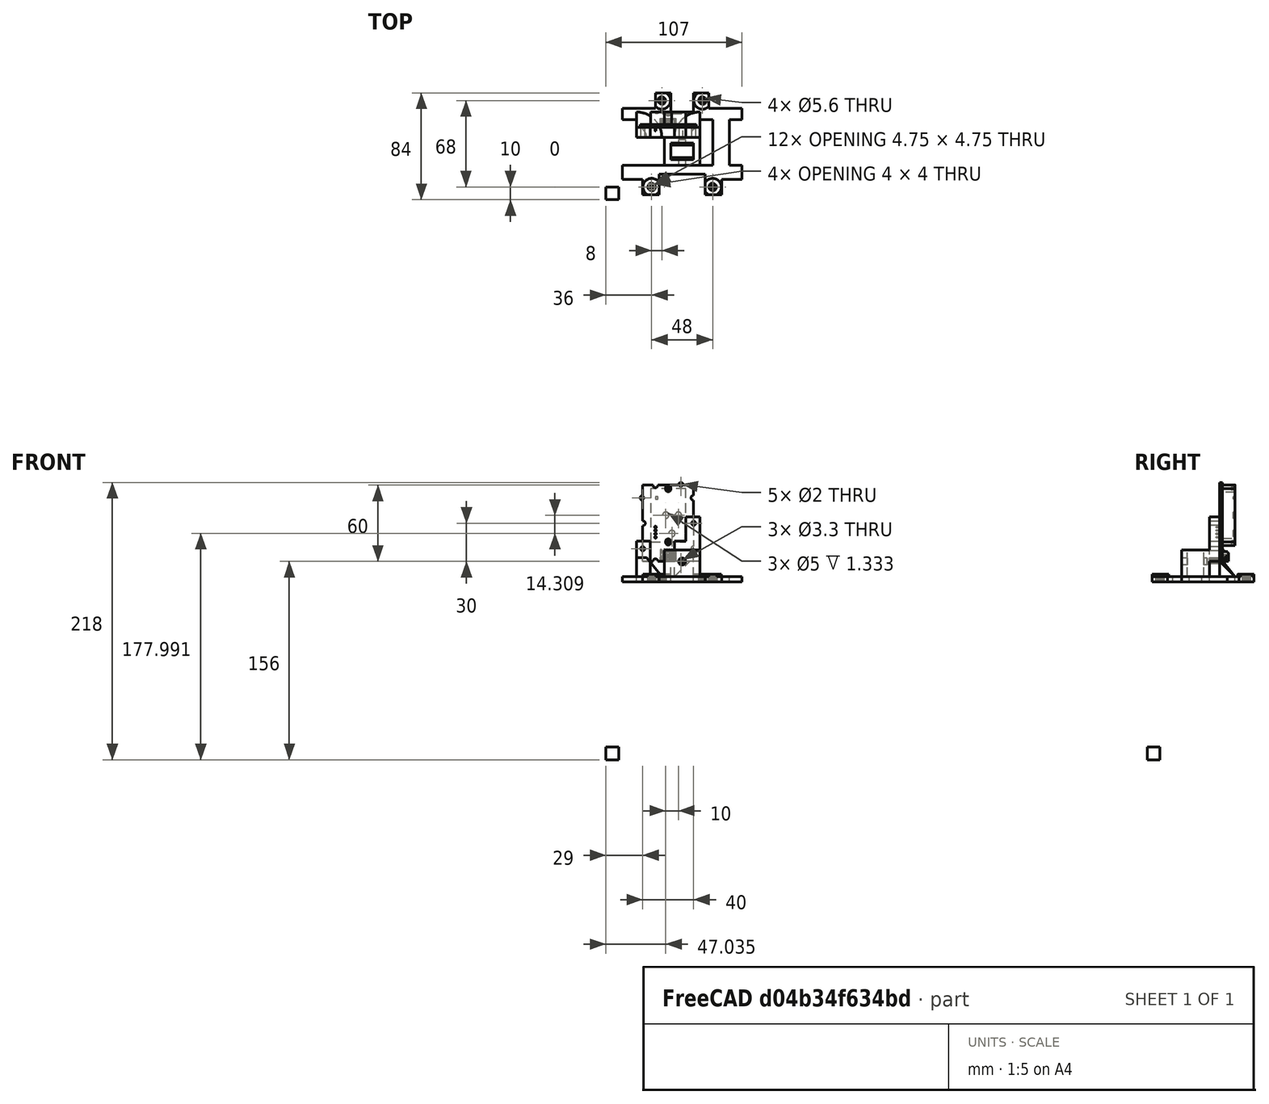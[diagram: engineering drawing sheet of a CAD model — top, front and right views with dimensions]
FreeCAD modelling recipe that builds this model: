
FCSTD DOCUMENT  (FreeCAD 0.20R29177 (Git))
Label: spin07122022
License: All rights reserved
LicenseURL: http://en.wikipedia.org/wiki/All_rights_reserved
objects: Part::Box×23, Part::Cylinder×17, Part::MultiFuse×12, Part::Feature×5, Part::Cut×3, Part::Cone×2
note: 62 computed .brp shape members not serialized (recipe doc carries the construction recipe); baked Part::Feature solids carry a one-line shape summary decoded from their .brp

FEATURE [Part::Cylinder] Cylinder103  label="Cylinder107"
  Angle = 360
  AttacherType = Attacher::AttachEngine3D
  FirstAngle = 0
  Height = 10
  Placement = pos=(63,3,0) rot=(0,0,1;0rad)
  Radius = 2.25
  SecondAngle = 0
FEATURE [Part::Box] Box064  label="base005"
  AttacherType = Attacher::AttachEngine3D
  Height = 4
  Length = 26
  Placement = pos=(-10.25,68,0) rot=(0,0,1;0rad)
  Width = 12
FEATURE [Part::Box] Box060  label="base001"
  AttacherType = Attacher::AttachEngine3D
  Height = 4
  Length = 94
  Width = 80
FEATURE [Part::Box] Box061  label="base002"
  AttacherType = Attacher::AttachEngine3D
  Height = 4
  Length = 26
  Width = 12
FEATURE [Part::Box] Box062  label="base003"
  AttacherType = Attacher::AttachEngine3D
  Height = 4
  Length = 26
  Placement = pos=(68,0,0) rot=(0,0,1;0rad)
  Width = 12
FEATURE [Part::Cylinder] Cylinder104  label="Cylinder103"
  Angle = 360
  AttacherType = Attacher::AttachEngine3D
  FirstAngle = 0
  Height = 10
  Placement = pos=(71,71,0) rot=(0,0,1;0rad)
  Radius = 2.25
  SecondAngle = 0
FEATURE [Part::Cylinder] Cylinder106  label="Cylinder104"
  Angle = 360
  AttacherType = Attacher::AttachEngine3D
  FirstAngle = 0
  Height = 10
  Placement = pos=(23,71,0) rot=(0,0,1;0rad)
  Radius = 2
  SecondAngle = 0
FEATURE [Part::Cylinder] Cylinder105  label="Cylinder108"
  Angle = 360
  AttacherType = Attacher::AttachEngine3D
  FirstAngle = 0
  Height = 10
  Placement = pos=(31,3,0) rot=(0,0,1;0rad)
  Radius = 2.25
  SecondAngle = 0
FEATURE [Part::Box] Box081  label="Cube039"
  AttacherType = Attacher::AttachEngine3D
  Height = 10
  Length = 10
  Placement = pos=(74,27,140) rot=(0,0,1;0rad)
  Width = 36
FEATURE [Part::Box] Box082  label="Cube040"
  AttacherType = Attacher::AttachEngine3D
  Height = 10
  Length = 36
  Placement = pos=(42,1,140) rot=(0,0,1;0rad)
  Width = 19
FEATURE [Part::Box] Box073  label="baseSpineCut"
  AttacherType = Attacher::AttachEngine3D
  Height = 25
  Length = 18
  Placement = pos=(51,33,140) rot=(0,0,1;0rad)
  Width = 10
FEATURE [Part::Cylinder] Cylinder107  label="Cylinder109"
  Angle = 360
  AttacherType = Attacher::AttachEngine3D
  FirstAngle = 0
  Height = 10
  Radius = 1
  SecondAngle = 0
FEATURE [Part::MultiFuse] Fusion123  label="screwIns001"
  Placement = pos=(0,3,0) rot=(0,0,1;0rad)
  Shapes = -> [Cylinder105,Cylinder107,Cylinder103,Cylinder104,Cylinder106]
FEATURE [Part::Box] Box080  label="Cube038"
  AttacherType = Attacher::AttachEngine3D
  Height = 10
  Length = 33
  Placement = pos=(13,27,140) rot=(0,0,1;0rad)
  Width = 22
FEATURE [Part::Box] Box063  label="base004"
  AttacherType = Attacher::AttachEngine3D
  Height = 4
  Length = 26
  Placement = pos=(78,68,0) rot=(0,0,1;0rad)
  Width = 12
FEATURE [Part::MultiFuse] Fusion122
  Shapes = -> [Box064,Box063,Box061,Box062]
FEATURE [Part::Cut] Cut019  label="baseNew"
  Base = -> Box060
  Tool = -> Fusion122
FEATURE [Part::Cut] Cut020  label="baseNew001"
  Base = -> Cut019
  Placement = pos=(107,84,140) rot=(0,0,1;3.14159rad)
  Tool = -> Fusion123
FEATURE [Part::Box] Box083  label="Cube041"
  AttacherType = Attacher::AttachEngine3D
  Height = 25
  Length = 18
  Placement = pos=(51,31.5,144) rot=(0,0,1;0rad)
  Width = 13
FEATURE [Part::Box] Box084  label="Cube042"
  AttacherType = Attacher::AttachEngine3D
  Height = 51
  Length = 50
  Placement = pos=(24,49,140) rot=(0,0,1;0rad)
  Width = 8
FEATURE [Part::Box] Box085  label="Cube043"
  AttacherType = Attacher::AttachEngine3D
  Height = 10
  Length = 15
  Placement = pos=(69,69,140) rot=(0,0,1;1.5708rad)
  Width = 18
FEATURE [Part::Box] Box086  label="baseSpineIn"
  AttacherType = Attacher::AttachEngine3D
  Height = 25
  Length = 28
  Placement = pos=(46,27,140) rot=(0,0,1;0rad)
  Width = 22
FEATURE [Part::Cylinder] Cylinder
  Angle = 360
  AttacherType = Attacher::AttachEngine3D
  FirstAngle = 0
  Height = 50
  Placement = pos=(60,-3,156) rot=(-1,0,0;1.5708rad)
  Radius = 2.8
  SecondAngle = 0
FEATURE [Part::Feature] Feature  label="Seed Grove SCD30"
  Placement = pos=(29,59,156) rot=(0.707107,0,0.707107;3.14159rad)
  shape: bbox 44 x 15.1 x 64 mm, 422 faces, 13 solids (baked)
FEATURE [Part::Cylinder] Cylinder108  label="Cylinder110"
  Angle = 360
  AttacherType = Attacher::AttachEngine3D
  FirstAngle = 0
  Height = 50
  Placement = pos=(80,17,186) rot=(-1,0,0;1.5708rad)
  Radius = 1.65
  SecondAngle = 0
FEATURE [Part::Cylinder] Cylinder109  label="Cylinder111"
  Angle = 360
  AttacherType = Attacher::AttachEngine3D
  FirstAngle = 0
  Height = 50
  Placement = pos=(40,17,166) rot=(-1,0,0;1.5708rad)
  Radius = 1.65
  SecondAngle = 0
FEATURE [Part::Cylinder] Cylinder110  label="Cylinder112"
  Angle = 360
  AttacherType = Attacher::AttachEngine3D
  FirstAngle = 0
  Height = 50
  Placement = pos=(70,17,156) rot=(-1,0,0;1.5708rad)
  Radius = 1.65
  SecondAngle = 0
FEATURE [Part::MultiFuse] Fusion  label="m2Cuts"
  Placement = pos=(-11,30,0) rot=(0,0,1;0rad)
  Shapes = -> [Cylinder108,Cylinder109,Cylinder110]
FEATURE [Part::Box] Box087  label="Cube044"
  AttacherType = Attacher::AttachEngine3D
  Height = 51
  Length = 50
  Placement = pos=(13,49,172) rot=(0,0,1;0rad)
  Width = 8
FEATURE [Part::Box] Box088  label="Cube045"
  AttacherType = Attacher::AttachEngine3D
  Height = 51
  Length = 19
  Placement = pos=(35,49,144) rot=(0,0,1;0rad)
  Width = 8
FEATURE [Part::MultiFuse] Fusion124  label="base"
  Shapes = -> [Cut020,Box084,Box086]
FEATURE [Part::MultiFuse] Fusion125  label="cuts"
  Shapes = -> [Box087,Box088,Fusion,Box085,Box080,Box083,Box082,Box081,Box073,Cylinder]
FEATURE [Part::Box] Box089  label="Cube046"
  AttacherType = Attacher::AttachEngine3D
  Height = 10
  Length = 11
  Placement = pos=(13,57,140) rot=(0,0,1;0rad)
  Width = 6
FEATURE [Part::Feature] Solid  label="m4HeatSet"
  Placement = pos=(36,10,140) rot=(1,0,0;1.5708rad)
  shape: bbox 7.1 x 7.1 x 6.065 mm, 234 faces (baked)
FEATURE [Part::Feature] Solid001  label="m4HeatSet001"
  Placement = pos=(84,10,140) rot=(1,0,0;1.5708rad)
  shape: bbox 7.1 x 7.1 x 6.065 mm, 234 faces (baked)
FEATURE [Part::Feature] Solid002  label="m4HeatSet002"
  Placement = pos=(44,78,140) rot=(1,0,0;1.5708rad)
  shape: bbox 7.1 x 7.1 x 6.065 mm, 234 faces (baked)
FEATURE [Part::Feature] Solid003  label="m4HeatSet003"
  Placement = pos=(76,78,140) rot=(1,0,0;1.5708rad)
  shape: bbox 7.1 x 7.1 x 6.065 mm, 234 faces (baked)
FEATURE [Part::Cylinder] Cylinder111  label="m4HeatSetCut"
  Angle = 360
  AttacherType = Attacher::AttachEngine3D
  FirstAngle = 0
  Height = 10
  Placement = pos=(36,10,140) rot=(0,0,1;0rad)
  Radius = 2.8
  SecondAngle = 0
FEATURE [Part::Cylinder] Cylinder112  label="m4HeatSetCut001"
  Angle = 360
  AttacherType = Attacher::AttachEngine3D
  FirstAngle = 0
  Height = 10
  Placement = pos=(84,10,140) rot=(0,0,1;0rad)
  Radius = 2.8
  SecondAngle = 0
FEATURE [Part::Cylinder] Cylinder113  label="m4HeatSetCut002"
  Angle = 360
  AttacherType = Attacher::AttachEngine3D
  FirstAngle = 0
  Height = 10
  Placement = pos=(76,78,140) rot=(0,0,1;0rad)
  Radius = 2.8
  SecondAngle = 0
FEATURE [Part::Cylinder] Cylinder114  label="m4HeatSetCut003"
  Angle = 360
  AttacherType = Attacher::AttachEngine3D
  FirstAngle = 0
  Height = 10
  Placement = pos=(44,78,140) rot=(0,0,1;0rad)
  Radius = 2.8
  SecondAngle = 0
FEATURE [Part::MultiFuse] Fusion126  label="heatSetCuts"
  Shapes = -> [Cylinder111,Cylinder112,Cylinder113,Cylinder114]
FEATURE [Part::Box] Box091  label="Cube048"
  AttacherType = Attacher::AttachEngine3D
  Height = 10
  Length = 11
  Placement = pos=(13,49,140) rot=(0,0,1;0rad)
  Width = 8
FEATURE [Part::MultiFuse] Fusion127  label="cuts001"
  Shapes = -> [Box091,Fusion126,Box089,Fusion125]
FEATURE [Part::Cylinder] Cylinder115  label="m4HeatSetCut004"
  Angle = 360
  AttacherType = Attacher::AttachEngine3D
  FirstAngle = 0
  Height = 6
  Placement = pos=(36,10,140) rot=(0,0,-1;1.0472rad)
  Radius = 6.8
  SecondAngle = 0
FEATURE [Part::Cylinder] Cylinder116  label="m4HeatSetCut005"
  Angle = 360
  AttacherType = Attacher::AttachEngine3D
  FirstAngle = 0
  Height = 6
  Placement = pos=(84,10,140) rot=(0,0,1;0rad)
  Radius = 6.8
  SecondAngle = 0
FEATURE [Part::Cylinder] Cylinder117  label="m4HeatSetCut006"
  Angle = 360
  AttacherType = Attacher::AttachEngine3D
  FirstAngle = 0
  Height = 6
  Placement = pos=(76,78,140) rot=(0,0,1;0rad)
  Radius = 6.8
  SecondAngle = 0
FEATURE [Part::Cylinder] Cylinder118  label="m4HeatSetCut007"
  Angle = 360
  AttacherType = Attacher::AttachEngine3D
  FirstAngle = 0
  Height = 6
  Placement = pos=(44,78,140) rot=(0,0,1;0rad)
  Radius = 6.8
  SecondAngle = 0
FEATURE [Part::MultiFuse] Fusion128  label="heatSetAddOns"
  Shapes = -> [Cylinder115,Cylinder116,Cylinder117,Cylinder118]
FEATURE [Part::Box] Box092  label="Cube049"
  AttacherType = Attacher::AttachEngine3D
  Height = 10
  Length = 94
  Placement = pos=(13,-4,140) rot=(0,0,1;0rad)
  Width = 8
FEATURE [Part::MultiFuse] Fusion129  label="base006"
  Shapes = -> [Fusion128,Fusion124]
FEATURE [Part::Box] Box093  label="Cube050"
  AttacherType = Attacher::AttachEngine3D
  Height = 10
  Length = 94
  Placement = pos=(13,84,140) rot=(0,0,1;0rad)
  Width = 8
FEATURE [Part::Box] Box094  label="Cube051"
  AttacherType = Attacher::AttachEngine3D
  Height = 10
  Length = 94
  Placement = pos=(89,72,140) rot=(0,0,1;1.5708rad)
  Width = 8
FEATURE [Part::Box] Box095  label="Cube052"
  AttacherType = Attacher::AttachEngine3D
  Height = 10
  Length = 94
  Placement = pos=(39,72,140) rot=(0,0,1;1.5708rad)
  Width = 8
FEATURE [Part::MultiFuse] Fusion130
  Shapes = -> [Box093,Box094,Box095,Box092]
FEATURE [Part::MultiFuse] Fusion131  label="cuts002"
  Shapes = -> [Fusion127,Fusion130]
FEATURE [Part::Box] Box096  label="Cube053"
  AttacherType = Attacher::AttachEngine3D
  Height = 10
  Length = 10
  Placement = pos=(97,27,140) rot=(0,0,1;0rad)
  Width = 36
FEATURE [Part::MultiFuse] Fusion132  label="cuts003"
  Shapes = -> [Fusion131,Box096]
FEATURE [Part::Cut] Cut  label="base007"
  Base = -> Fusion129
  Tool = -> Fusion132
FEATURE [Part::Cone] Cone
  Angle = 90
  AttacherType = Attacher::AttachEngine3D
  Height = 15
  Placement = pos=(24,49,144) rot=(0,0,1;0rad)
  Radius1 = 20
  Radius2 = 8
FEATURE [Part::Cone] Cone001
  Angle = 90
  AttacherType = Attacher::AttachEngine3D
  Height = 12
  Placement = pos=(74,49,144) rot=(0,0,1;1.5708rad)
  Radius1 = 20
  Radius2 = 8
FEATURE [Part::Box] Box  label="Cube"
  AttacherType = Attacher::AttachEngine3D
  Height = 10
  Length = 10
  Width = 10
